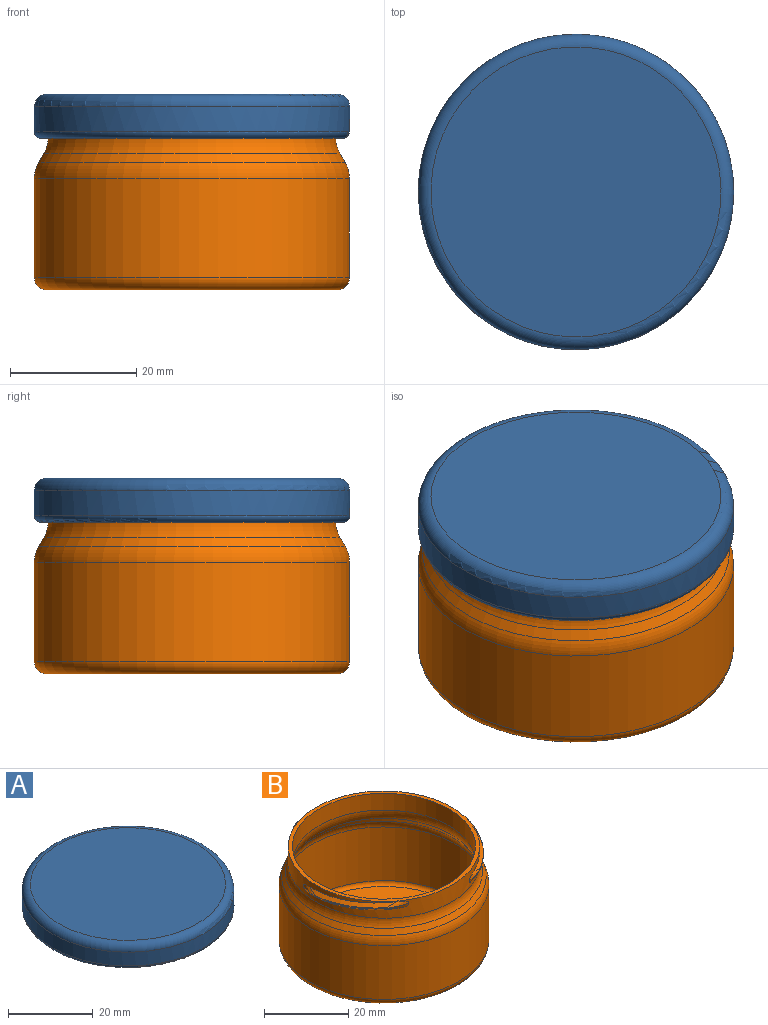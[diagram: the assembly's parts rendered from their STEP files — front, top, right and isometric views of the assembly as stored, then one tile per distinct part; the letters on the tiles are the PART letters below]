
ASSEMBLY  parts=2 mates=1
PART A: 46 faces, bbox 54.1x54.1x7.4 mm
  f0: bspline ~32.78x14.18mm, area 30.9mm2, adj f1,f3,f19,f23,f24
  f1: bspline ~31.61x13.3mm, area 7.2mm2, adj f0,f2,f20,f24
  f2: bspline ~32.78x14.18mm, area 30.9mm2, adj f1,f3,f20,f22,f26
  f3: cylinder r=24mm len=48mm, axis (0,0,-1), area 575.3mm2, adj f0,f2,f4,f6,f7,f9,f13,f14
  f4: bspline ~32.78x14.18mm, area 30.9mm2, adj f3,f5,f27,f31,f32
  f5: bspline ~31.61x13.3mm, area 7.2mm2, adj f4,f6,f28,f32
  f6: bspline ~32.78x14.18mm, area 30.9mm2, adj f3,f5,f28,f30,f34
  f7: bspline ~24x24mm, area 30.9mm2, adj f3,f8,f35,f39,f40
  f8: bspline ~23.14x23.14mm, area 7.2mm2, adj f7,f9,f36,f40
  f9: bspline ~24x24mm, area 30.9mm2, adj f3,f8,f36,f38,f42
  f10: cylinder r=25mm len=50mm, axis (0,0,-1), area 628.3mm2, adj f43,f45
  f11: plane 46x46mm, normal (0,0,1), area 1661.9mm2, adj f43
  f12: plane 46x46mm, normal (0,0,-1), area 1661.9mm2, adj f44
  f13: plane 0.27x0.21mm, normal (-0.74,-0.67,0), area 0mm2, adj f3,f39,f42
  f14: plane 0.27x0.25mm, normal (-0.87,-0.5,0), area 0mm2, adj f3,f35,f38
  f15: plane 0.28x0.27mm, normal (-0.21,0.98,0), area 0mm2, adj f3,f31,f34
  f16: plane 0.29x0.27mm, normal (0,1,0), area 0mm2, adj f3,f27,f30
  f17: plane 0.27x0.27mm, normal (0.95,-0.31,0), area 0mm2, adj f3,f23,f26
  f18: plane 0.27x0.25mm, normal (0.87,-0.5,0), area 0mm2, adj f3,f19,f22
  f19: bspline ~3.31x2.83mm, area 2.2mm2, adj f0,f3,f18,f20,f21
  f20: bspline ~0.56x0.49mm, area 0mm2, adj f1,f2,f19,f21
  f21: bspline ~2.5x2.21mm, area 0.3mm2, adj f19,f20,f22
  f22: bspline ~3.01x2.37mm, area 2mm2, adj f2,f3,f18,f21
  f23: bspline ~3.5x2.31mm, area 1.9mm2, adj f0,f3,f17,f25
  f24: bspline ~0.63x0.29mm, area 0mm2, adj f0,f1,f25,f26
  f25: bspline ~3.23x0.47mm, area 0.3mm2, adj f23,f24,f26
  f26: bspline ~3.94x2.82mm, area 2.2mm2, adj f2,f3,f17,f24,f25
  f27: bspline ~4.01x2.83mm, area 2.2mm2, adj f3,f4,f16,f28,f29
  f28: bspline ~0.78x0.42mm, area 0mm2, adj f5,f6,f27,f29
  f29: bspline ~3.21x0.75mm, area 0.3mm2, adj f27,f28,f30
  f30: bspline ~3.62x2.37mm, area 2mm2, adj f3,f6,f16,f29
  f31: bspline ~3.32x2.31mm, area 1.9mm2, adj f3,f4,f15,f33
  f32: bspline ~0.59x0.45mm, area 0mm2, adj f4,f5,f33,f34
  f33: bspline ~3.02x1.38mm, area 0.3mm2, adj f31,f32,f34
  f34: bspline ~3.75x2.82mm, area 2.2mm2, adj f3,f6,f15,f32,f33
  f35: bspline ~3.76x2.83mm, area 2.2mm2, adj f3,f7,f14,f36,f37
  f36: bspline ~0.81x0.3mm, area 0mm2, adj f8,f9,f35,f37
  f37: bspline ~3.08x1.11mm, area 0.3mm2, adj f35,f36,f38
  f38: bspline ~3.4x2.37mm, area 2mm2, adj f3,f9,f14,f37
  f39: bspline ~2.74x2.53mm, area 1.9mm2, adj f3,f7,f13,f41
  f40: bspline ~0.78x0.49mm, area 0mm2, adj f7,f8,f41,f42
  f41: bspline ~2.64x2.01mm, area 0.3mm2, adj f39,f40,f42
  f42: bspline ~3.08x2.82mm, area 2.2mm2, adj f3,f9,f13,f40,f41
  f43: torus R=23mm, axis (0,0,1), area 479.1mm2, adj f10,f11
  f44: torus R=23mm, axis (0,0,1), area 233.3mm2, adj f3,f12
  f45: torus R=24mm, axis (0,0,-1), area 243.2mm2, adj f3,f10
PART B: 54 faces, bbox 54.1x54.1x29.6 mm
  f0: bspline ~32.32x13.99mm, area 25.5mm2, adj f1,f10,f29,f32,f36
  f1: bspline ~32.43x13.65mm, area 5.9mm2, adj f0,f2,f29,f35
  f2: bspline ~32.32x13.99mm, area 25.5mm2, adj f1,f10,f30,f33,f35
  f3: bspline ~32.32x13.99mm, area 25.5mm2, adj f4,f10,f37,f40,f44
  f4: bspline ~32.43x13.65mm, area 5.9mm2, adj f3,f5,f37,f43
  f5: bspline ~32.32x13.99mm, area 25.5mm2, adj f4,f10,f38,f41,f43
  f6: bspline ~23.66x23.66mm, area 25.5mm2, adj f7,f10,f45,f48,f52
  f7: bspline ~23.74x23.74mm, area 5.9mm2, adj f6,f8,f45,f51
  f8: bspline ~23.66x23.66mm, area 25.5mm2, adj f7,f10,f46,f49,f51
  f9: torus R=27.8mm, axis (0,0,-1), area 378.8mm2, adj f10,f22
  f10: cylinder r=22.8mm len=45.6mm, axis (0,0,-1), area 528.7mm2, adj f0,f2,f3,f5,f6,f8,f9,f11
  f11: plane 45.6x45.6mm, normal (0,0,1), area 140.1mm2, adj f10,f12
  f12: cylinder r=21.8mm len=43.6mm, axis (0,0,-1), area 664.3mm2, adj f11,f13
  f13: torus R=27.8mm, axis (0,0,-1), area 435.7mm2, adj f12,f14
  f14: cone r=23.46mm half-angle=30deg, axis (0,0,-1), area 249mm2, adj f13,f15
  f15: torus R=20mm, axis (0,0,-1), area 313.5mm2, adj f14,f16
  f16: cylinder r=24mm len=48mm, axis (0,0,-1), area 2361.5mm2, adj f15,f17
  f17: torus R=23mm, axis (0,0,-1), area 233.3mm2, adj f16,f18
  f18: plane 46x46mm, normal (0,0,1), area 1661.9mm2, adj f17
  f19: plane 46x46mm, normal (0,0,-1), area 1661.9mm2, adj f53
  f20: cylinder r=25mm len=50mm, axis (0,0,-1), area 2459.9mm2, adj f21,f53
  f21: torus R=20mm, axis (0,0,-1), area 407.5mm2, adj f20,f22
  f22: cone r=24.33mm half-angle=30deg, axis (0,0,-1), area 258.4mm2, adj f9,f21
  f23: plane 0.65x0.27mm, normal (0.14,-0.99,0), area 0.1mm2, adj f10,f49,f52
  f24: plane 0.65x0.27mm, normal (0.98,0.17,0), area 0.1mm2, adj f10,f46,f48
  f25: plane 0.61x0.27mm, normal (-0.93,0.37,0), area 0.1mm2, adj f10,f41,f44
  f26: plane 0.62x0.27mm, normal (-0.34,-0.94,0), area 0.1mm2, adj f10,f38,f40
  f27: plane 0.52x0.41mm, normal (0.79,0.62,0), area 0.1mm2, adj f10,f33,f36
  f28: plane 0.51x0.42mm, normal (-0.64,0.77,0), area 0.1mm2, adj f10,f30,f32
  f29: bspline ~0.86x0.42mm, area 0.1mm2, adj f0,f1,f30,f31
  f30: bspline ~4.97x3.87mm, area 4.1mm2, adj f2,f10,f28,f29,f31
  f31: bspline ~4.25x2.68mm, area 0.4mm2, adj f29,f30,f32
  f32: bspline ~5.24x4.26mm, area 2.7mm2, adj f0,f10,f28,f31
  f33: bspline ~6.74x5.65mm, area 2.7mm2, adj f2,f10,f27,f34
  f34: bspline ~3.9x3.64mm, area 0.4mm2, adj f33,f35,f36
  f35: bspline ~0.84x0.56mm, area 0.1mm2, adj f1,f2,f34,f36
  f36: bspline ~6.02x5.31mm, area 4.2mm2, adj f0,f10,f27,f34,f35
  f37: bspline ~0.74x0.66mm, area 0.1mm2, adj f3,f4,f38,f39
  f38: bspline ~5.28x3.29mm, area 4.1mm2, adj f5,f10,f26,f37,f39
  f39: bspline ~4.65x2.65mm, area 0.4mm2, adj f37,f38,f40
  f40: bspline ~5.76x2.78mm, area 2.7mm2, adj f3,f10,f26,f39
  f41: bspline ~7.96x3.57mm, area 2.7mm2, adj f5,f10,f25,f42
  f42: bspline ~5.14x1.26mm, area 0.4mm2, adj f41,f43,f44
  f43: bspline ~0.89x0.31mm, area 0.1mm2, adj f4,f5,f42,f44
  f44: bspline ~7.11x3.6mm, area 4.2mm2, adj f3,f10,f25,f42,f43
  f45: bspline ~0.87x0.29mm, area 0.1mm2, adj f6,f7,f46,f47
  f46: bspline ~5.91x3.29mm, area 4.1mm2, adj f8,f10,f24,f45,f47
  f47: bspline ~5.29x0.44mm, area 0.4mm2, adj f45,f46,f48
  f48: bspline ~6.3x2.78mm, area 2.7mm2, adj f6,f10,f24,f47
  f49: bspline ~8.2x2.91mm, area 2.7mm2, adj f8,f10,f23,f50
  f50: bspline ~5.07x1.65mm, area 0.4mm2, adj f49,f51,f52
  f51: bspline ~0.83x0.57mm, area 0.1mm2, adj f7,f8,f50,f52
  f52: bspline ~7.19x3.6mm, area 4.2mm2, adj f6,f10,f23,f50,f51
  f53: torus R=23mm, axis (0,0,-1), area 479.1mm2, adj f19,f20
PLACE A rot(axis=(0,0,-1),97.6deg) t=(-13.08,20,26.91)mm
PLACE B rot(axis=(0,0,-1),147.6deg) t=(-13.08,20,2.85)mm
MATE cylindrical B.f9 <-> A.f3  axis (0,0,-1) through (-13.08,20,12.68)mm
